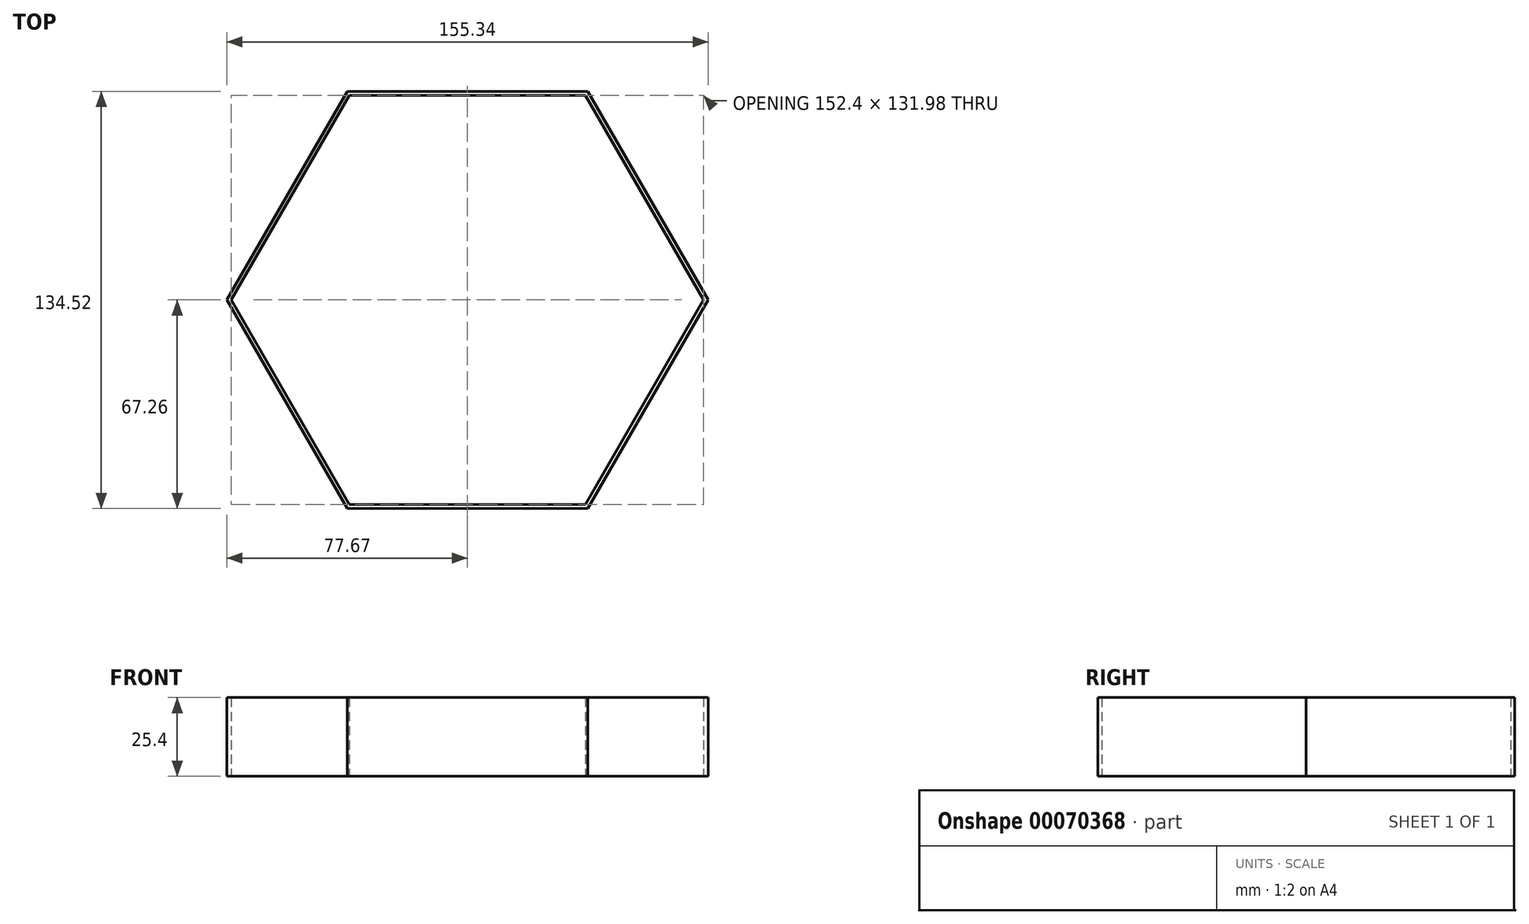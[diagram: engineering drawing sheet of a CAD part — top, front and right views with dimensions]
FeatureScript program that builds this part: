
annotation { "Feature Type Name" : "Feature", "Feature Type Description" : "" }
export const myFeature = defineFeature(function(context is Context, id is Id, definition is map)
    precondition{}
    {
        {
            var Q0;
            Q0=qCreatedBy(makeId("Top.planeOp"),FACE);
            var sketch = newSketch(context, id + "F0", { "sketchPlane" : qUnion([Q0])});
            skCircle(sketch, "E0.cCircle", {"center": v(0, 0) * mm, "radius": 66 * mm, "construction": true});
            skLineSegment(sketch, "E0.0", {"start": v(76.2, 0) * mm, "end": v(38.1, -66) * mm});
            skLineSegment(sketch, "E0.1", {"start": v(38.1, -66) * mm, "end": v(-38.1, -66) * mm});
            skLineSegment(sketch, "E0.2", {"start": v(-38.1, -66) * mm, "end": v(-76.2, 0) * mm});
            skLineSegment(sketch, "E0.3", {"start": v(-76.2, 0) * mm, "end": v(-38.1, 66) * mm});
            skLineSegment(sketch, "E0.4", {"start": v(-38.1, 66) * mm, "end": v(38.1, 66) * mm});
            skLineSegment(sketch, "E0.5", {"start": v(38.1, 66) * mm, "end": v(76.2, 0) * mm});
            skPoint(sketch, "E0.0.midPoint", {"position": v(57.15, -33) * mm});
            skCircle(sketch, "E1.cCircle", {"center": v(0, 0) * mm, "radius": 67.26 * mm, "construction": true});
            skLineSegment(sketch, "E1.0", {"start": v(77.67, 0) * mm, "end": v(38.83, -67.26) * mm});
            skLineSegment(sketch, "E1.1", {"start": v(38.83, -67.26) * mm, "end": v(-38.83, -67.26) * mm});
            skLineSegment(sketch, "E1.2", {"start": v(-38.83, -67.26) * mm, "end": v(-77.67, 0) * mm});
            skLineSegment(sketch, "E1.3", {"start": v(-77.67, 0) * mm, "end": v(-38.83, 67.26) * mm});
            skLineSegment(sketch, "E1.4", {"start": v(-38.83, 67.26) * mm, "end": v(38.83, 67.26) * mm});
            skLineSegment(sketch, "E1.5", {"start": v(38.83, 67.26) * mm, "end": v(77.67, 0) * mm});
            skPoint(sketch, "E1.0.midPoint", {"position": v(58.25, -33.63) * mm});
            skSolve(sketch);
        }
        {
            var Q0;
            Q0 = qSketchRegion(id + "F0", true);
            extrude(context, id + "F1", {"entities" : qUnion([Q0]), "depth" : 25.4 * mm});
        }
    });
